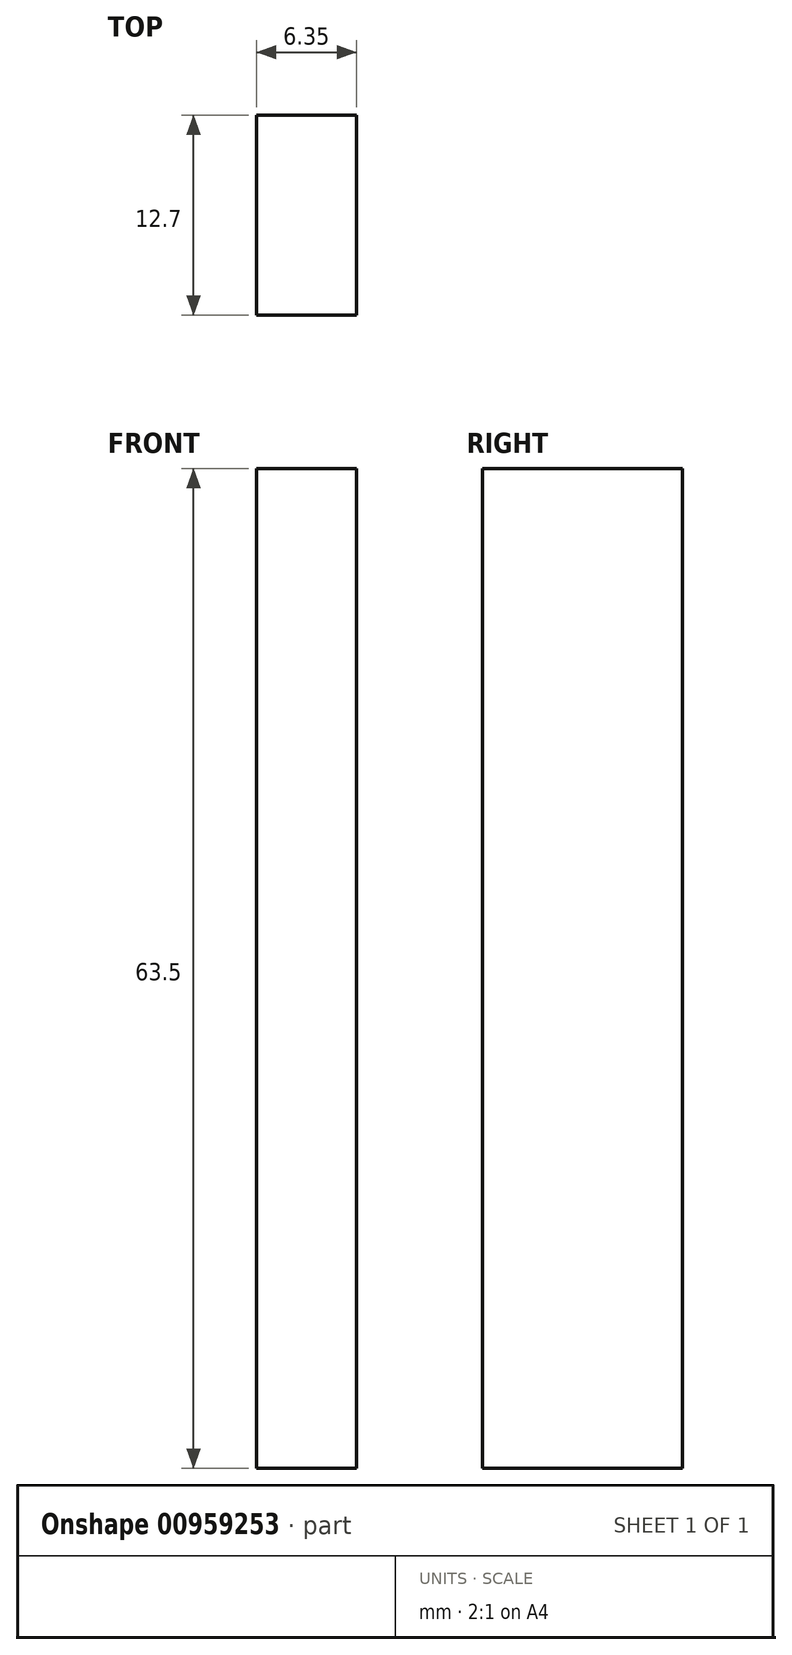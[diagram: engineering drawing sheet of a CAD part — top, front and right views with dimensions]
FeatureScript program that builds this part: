
annotation { "Feature Type Name" : "Feature", "Feature Type Description" : "" }
export const myFeature = defineFeature(function(context is Context, id is Id, definition is map)
    precondition{}
    {
        {
            var Q0;
            Q0=qCreatedBy(makeId("Front.planeOp"),FACE);
            var sketch = newSketch(context, id + "F0", { "sketchPlane" : qUnion([Q0])});
            skLineSegment(sketch, "E0", {"start": v(0, 0) * mm, "end": v(0, 63.5) * mm});
            skLineSegment(sketch, "E1", {"start": v(0, 63.5) * mm, "end": v(6.35, 63.5) * mm});
            skLineSegment(sketch, "E2", {"start": v(6.35, 63.5) * mm, "end": v(6.35, 0) * mm});
            skLineSegment(sketch, "E3", {"start": v(6.35, 0) * mm, "end": v(0, 0) * mm});
            skSolve(sketch);
        }
        {
            var Q0;
            Q0=makeQuery(id+"F0.imprint","IMPRINT",FACE,{"disambiguationData":[TD([[makeQuery(id+"F0.imprint","IMPRINT",EDGE,{"derivedFrom":sQuery(id+"F0.wireOp",EDGE,"E0")}),-1.0]])]});
            extrude(context, id + "F1", {"entities" : qUnion([Q0]), "oppositeDirection" : true, "depth" : 12.7 * mm, "offsetDistance" : 25.4 * mm});
        }
    });
